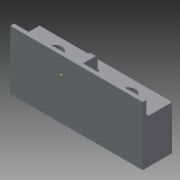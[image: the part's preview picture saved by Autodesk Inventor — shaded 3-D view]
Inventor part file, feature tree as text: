
AUTODESK INVENTOR PART (.ipt)
format: ipt  version: 2015 (Build 190159000, 159)  size: 129,024 bytes
history: native  units: mm
features: sketch x5, extrude x4, fillet x2
ambient origin geometry x8: Origin, YZ Plane, XZ Plane, XY Plane, X Axis, Y Axis, Z Axis, Center Point
bodies: Solid1 (feature_tree)
feature tree (11):
  extrude  "Extrusion1"  Depth=5.2mm
  extrude  "Extrusion2"  Depth=5.0mm
  sketch  "Sketch3"  dims[d4=5.0mm d5=10.0mm]
  extrude  "Extrusion3"  Depth=10.0mm
  extrude  "Extrusion4"  Depth=10.0mm
  fillet  "Fillet1"  Radius=25.0mm
  fillet  "Fillet2"  Radius=15.0mm
  sketch  "Sketch1"  dims[d0=5.2mm d1=5.2mm]
  sketch  "Sketch2"  dims[d2=10.0mm d3=5.0mm]
  sketch  "Sketch4"  dims[d6=45.0mm d7=10.0mm d8=25.0mm d9=15.0mm d10=0.0mm]
  sketch  "Sketch5"  dims[d11=5.0mm d12=0.0mm d13=2.0mm d14=3.0mm d15=21.5mm d16=2.0mm d17=21.5mm d18=5.0mm d19=0.0mm d20=2.0mm d21=4.0mm d22=0.0mm d23=1.0mm d24=1.0mm]
